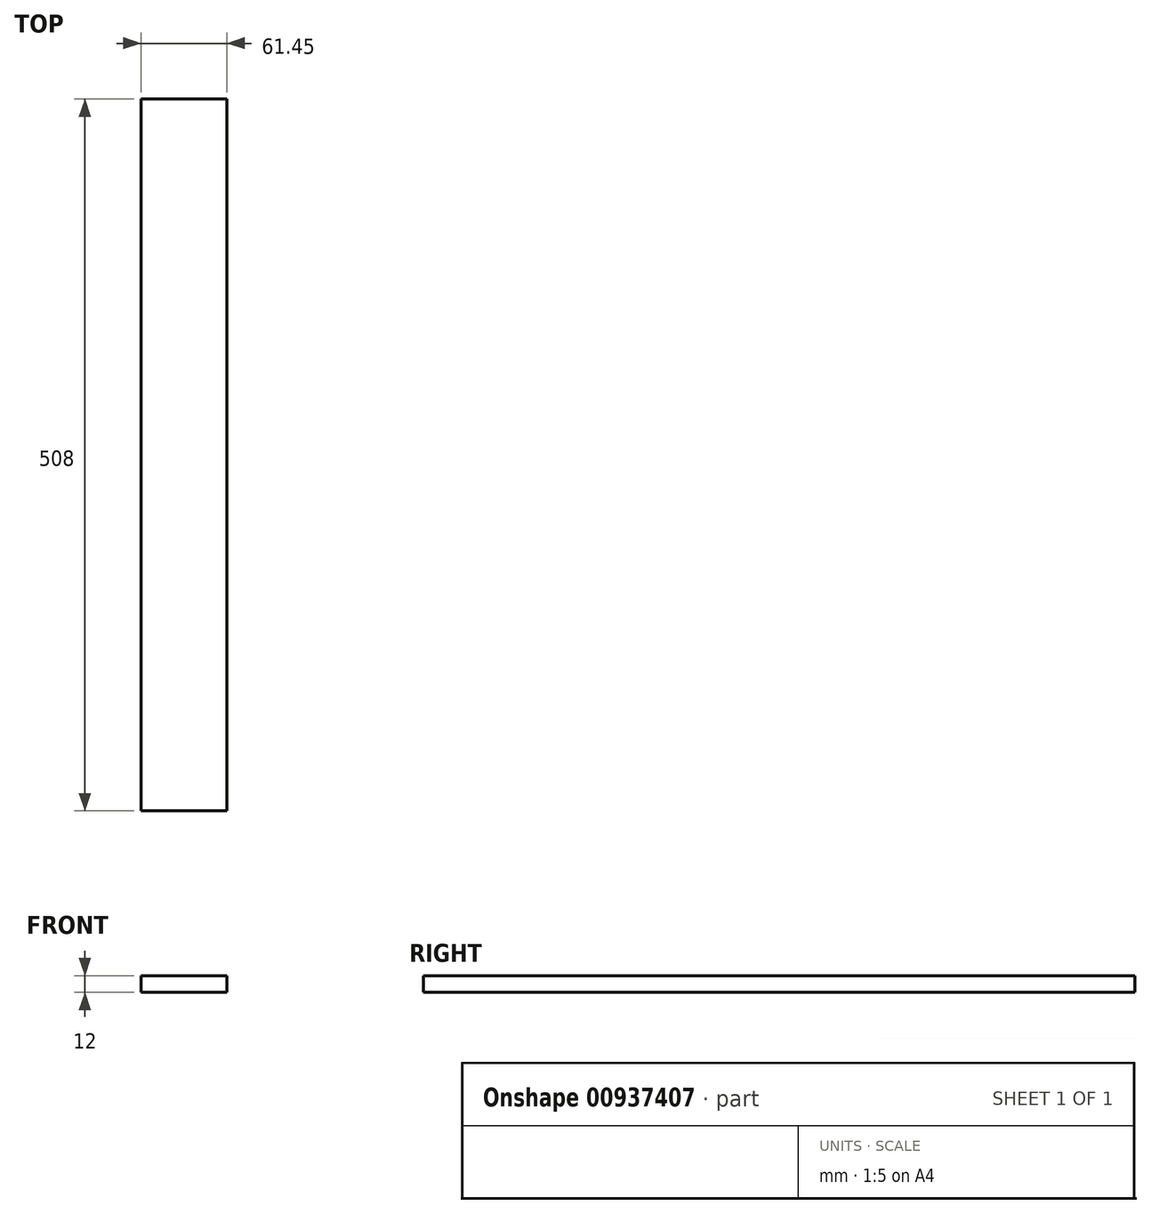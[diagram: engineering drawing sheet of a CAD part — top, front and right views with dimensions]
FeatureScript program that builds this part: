
annotation { "Feature Type Name" : "Feature", "Feature Type Description" : "" }
export const myFeature = defineFeature(function(context is Context, id is Id, definition is map)
    precondition{}
    {
        {
            var Q0;
            Q0=qCreatedBy(makeId("Front.planeOp"),FACE);
            var sketch = newSketch(context, id + "F0", { "sketchPlane" : qUnion([Q0])});
            skLineSegment(sketch, "E0.bottom", {"start": v(0, 0) * mm, "end": v(61.45, 0) * mm});
            skLineSegment(sketch, "E0.top", {"start": v(0, -12) * mm, "end": v(61.45, -12) * mm});
            skLineSegment(sketch, "E0.left", {"start": v(0, 0) * mm, "end": v(0, -12) * mm});
            skLineSegment(sketch, "E0.right", {"start": v(61.45, 0) * mm, "end": v(61.45, -12) * mm});
            skSolve(sketch);
        }
        {
            var Q0;
            Q0 = qSketchRegion(id + "F0", true);
            extrude(context, id + "F1", {"entities" : qUnion([Q0]), "depth" : 508 * mm, "offsetDistance" : 25.4 * mm});
        }
    });
